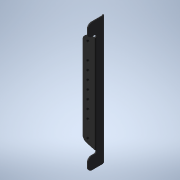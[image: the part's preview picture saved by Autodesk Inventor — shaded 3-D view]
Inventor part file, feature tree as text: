
AUTODESK INVENTOR PART (.ipt)
format: ipt  version: 2021 (Build 250183000, 183)  size: 271,360 bytes
history: native  units: mm
features: other x21, sketch x11, extrude x9, pattern_linear x2, revolve x1, hole x1, fillet x1
ambient origin geometry x8: Origin, YZ Plane, XZ Plane, XY Plane, X Axis, Y Axis, Z Axis, Center Point
bodies: Solid1 (feature_tree)
feature tree (46):
  extrude  "Extrusion1"  Depth=110.0mm TaperAngle=0.0deg
  extrude  "Extrusion2"  Depth=5.0mm TaperAngle=0.0deg
  extrude  "Extrusion3"  Depth=2.5mm TaperAngle=0.0deg
  extrude  "Extrusion4"  TaperAngle=360.0deg  [1 undecoded]
  extrude  "Extrusion5"  Depth=12.5mm TaperAngle=0.0deg
  extrude  "Extrusion6"  Depth=1.7mm TaperAngle=0.0deg
  extrude  "Extrusion7"  TaperAngle=0.0deg  [1 undecoded]
  revolve  "Revolution1"  [1 undecoded]
  pattern_linear  "Rectangular Pattern1"  [2 undecoded]
  hole  "Hole1"  [1 undecoded]
  pattern_linear  "Rectangular Pattern2"  [2 undecoded]
  extrude  "Extrusion8"  [1 undecoded]
  extrude  "Extrusion9"  [1 undecoded]
  fillet  "Fillet1"  [1 undecoded]
  other  "SC1_XY"
  other  "SC1_YZ"
  other  "SC1_ZX"
  other  "SC1_X"
  other  "SC1_Y"
  other  "SC1_Z"
  other  "SC1_Center"
  other  "SC2_XY"
  other  "SC2_YZ"
  other  "SC2_ZX"
  other  "SC2_X"
  other  "SC2_Y"
  other  "SC2_Z"
  other  "SC2_Center"
  other  "SEITENTEIL_XY"
  other  "SEITENTEIL_YZ"
  other  "SEITENTEIL_ZX"
  other  "SEITENTEIL_X"
  other  "SEITENTEIL_Y"
  other  "SEITENTEIL_Z"
  other  "SEITENTEIL_Center"
  sketch  "Sketch_1"  dims[d0=190.0mm d1=0.0mm d2=110.0mm d3=0.0mm]
  sketch  "Sketch_2"  dims[d4=110.0mm d5=0.0mm d6=5.0mm d7=0.0mm]
  sketch  "Sketch_3"  dims[d8=2.5mm d9=0.0mm d10=148.0mm d11=0.0mm]
  sketch  "Sketch_5"  dims[d12=196.0mm d13=0.0mm d14=360.0deg]
  sketch  "Sketch_91"
  sketch  "Sketch_6"  dims[d15=110.0mm d17=12.5mm d18=10.0mm d20=0.0mm]
  sketch  "Sketch_9"  dims[d34=1.5mm d35=0.0mm d36=1.7mm d37=0.0mm]
  sketch  "Sketch_7"  dims[d21=4.6mm d22=6.0mm d23=4.0mm d24=2.0mm d25=90.0deg d26=3.2mm d27=0.0mm d28=110.0mm d30=12.5mm d31=10.0mm d33=0.0mm]
  sketch  "Sketch9"  dims[d38=8.0mm d39=0.0mm d40=0.0mm d41=0.0mm]
  sketch  "Sketch_105"
  sketch  "Sketch_106"
note: 11 required parameter values undecoded (feature->parameter linkage not recoverable at this tier; creation-order binding heuristic only, values carry confidence <= 0.55)
